# Revit family: Triomax_TDLP76×2000×4-250×5
name_source: partatom
category: Generic Models
units: mm (PartAtom-declared; Revit-internal decimal feet)

## family parameters
Always vertical = Yes
Can host rebar = No
Cut with Voids When Loaded = No
Maintain Annotation Orientation = No
Part Type = Normal
Room Calculation Point = No
Round Connector Dimension = Use Diameter
Shared = No
Work Plane-Based = No

## types (1)
- Triomax_TDLP76×2000×4-250×5
    Default Elevation = 0 mm  [stored 0 ft]
    Length = 2000 mm  [stored 6.56168 ft]
    Load capacity = (vertical, Pull-out, Horizontal-Indicative only)
    Manufacturer = ROCKBASE
    Material Specs = S355B
    Model = WBQ TDLP76×2000×4-250×5
    Outer diameter = 76 mm  [stored 0.249344 ft]
    URL = https://www.rockbase.co.il
    Wall Thikness = 4 mm  [stored 0.0131234 ft]

note: [stored X ft] marks values corroborated as IEEE doubles in the binary element streams (Revit-internal decimal feet)

## geometry (parser evidence)
native form markers: Sweep x5
no freeform markers — native parametric forms only
